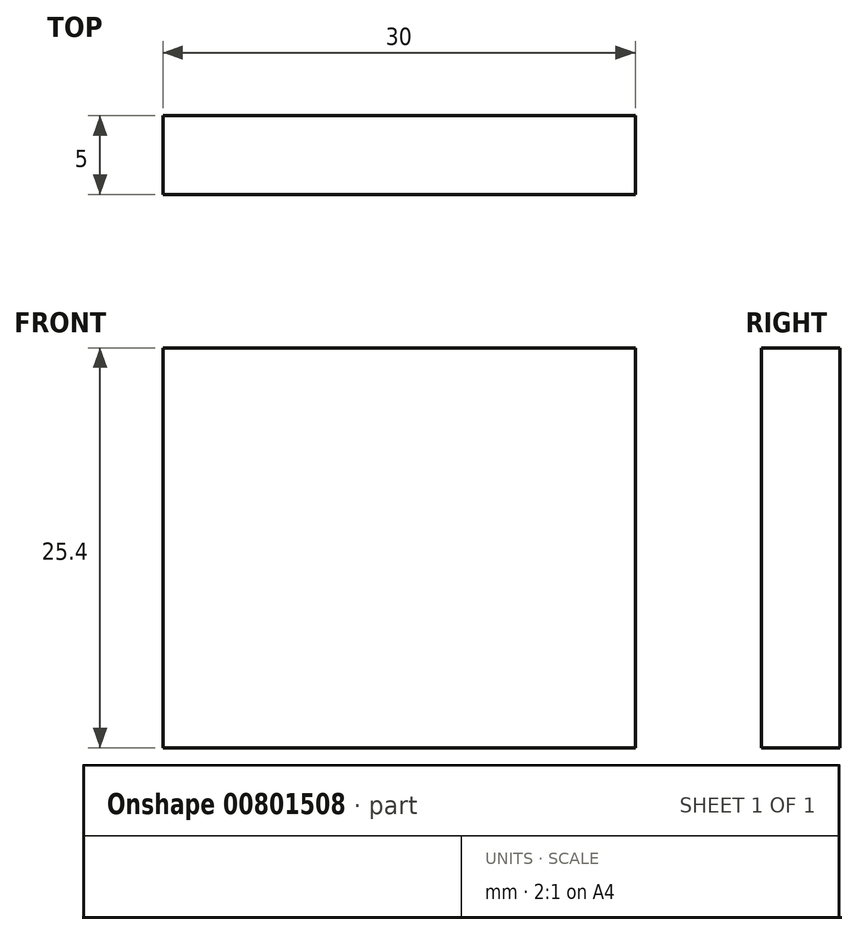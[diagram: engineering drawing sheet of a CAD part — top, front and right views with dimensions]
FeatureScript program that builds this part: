
annotation { "Feature Type Name" : "Feature", "Feature Type Description" : "" }
export const myFeature = defineFeature(function(context is Context, id is Id, definition is map)
    precondition{}
    {
        {
            var Q0;
            Q0=qCreatedBy(makeId("Top.planeOp"),FACE);
            var sketch = newSketch(context, id + "F0", { "sketchPlane" : qUnion([Q0])});
            skLineSegment(sketch, "E0.bottom", {"start": v(-15, 2.5) * mm, "end": v(15, 2.5) * mm});
            skLineSegment(sketch, "E0.top", {"start": v(-15, -2.5) * mm, "end": v(15, -2.5) * mm});
            skLineSegment(sketch, "E0.left", {"start": v(-15, 2.5) * mm, "end": v(-15, -2.5) * mm});
            skLineSegment(sketch, "E0.right", {"start": v(15, 2.5) * mm, "end": v(15, -2.5) * mm});
            skPoint(sketch, "E0.middle", {"position": v(0, 0) * mm});
            skSolve(sketch);
        }
        {
            var Q0;
            Q0 = qSketchRegion(id + "F0", true);
            extrude(context, id + "F1", {"entities" : qUnion([Q0]), "depth" : 25.4 * mm, "offsetDistance" : 25.4 * mm});
        }
    });
